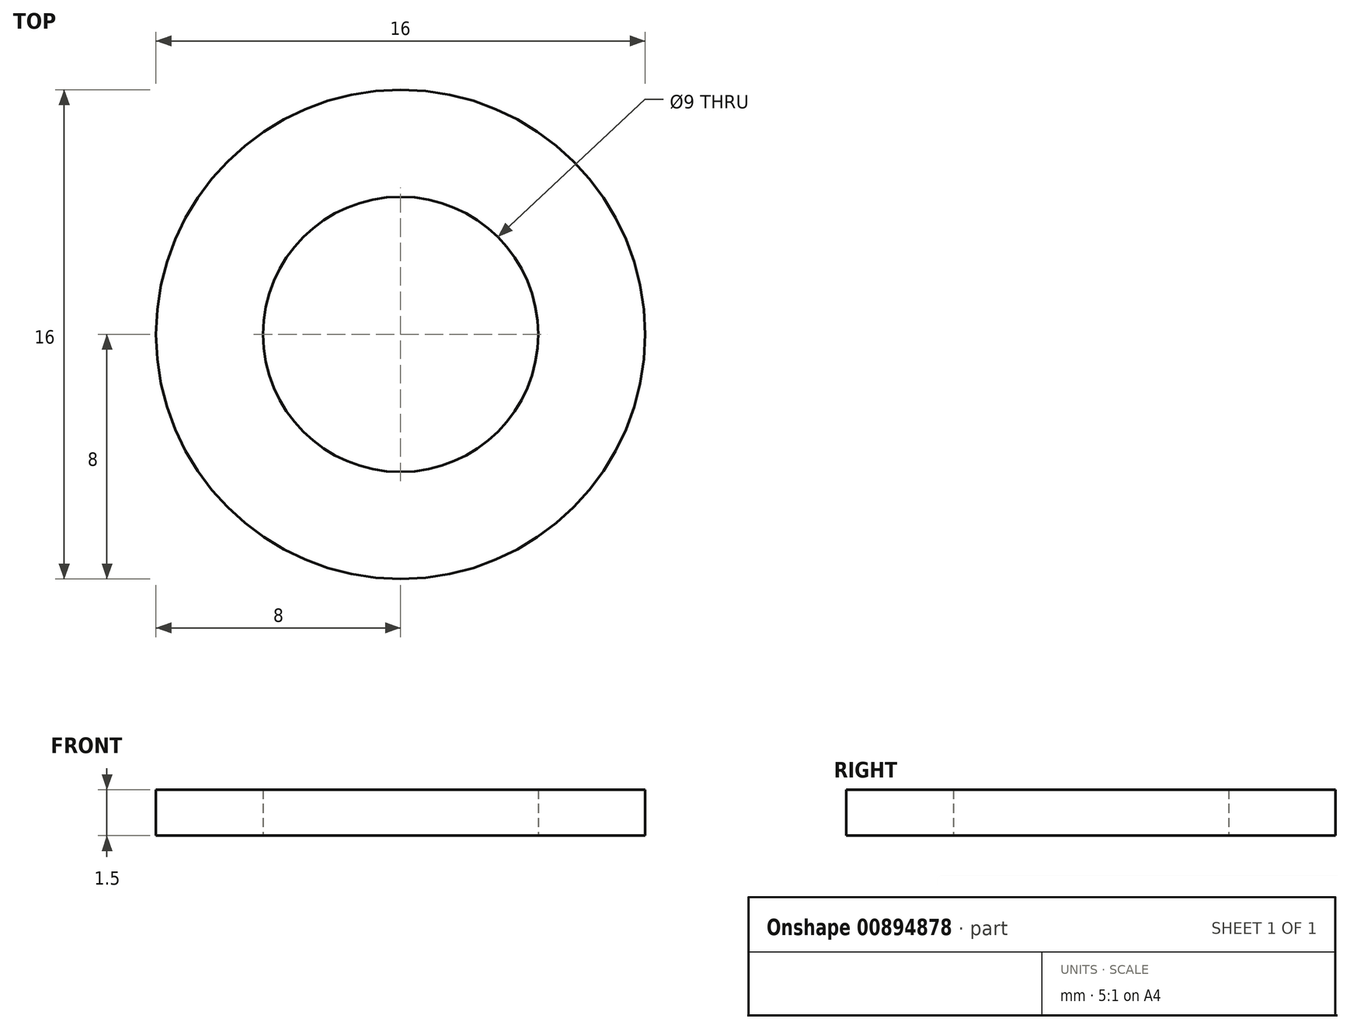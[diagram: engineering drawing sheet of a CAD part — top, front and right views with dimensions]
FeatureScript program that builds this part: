
annotation { "Feature Type Name" : "Feature", "Feature Type Description" : "" }
export const myFeature = defineFeature(function(context is Context, id is Id, definition is map)
    precondition{}
    {
        {
            var Q0;
            Q0=qCreatedBy(makeId("Top.planeOp"),FACE);
            var sketch = newSketch(context, id + "F0", { "sketchPlane" : qUnion([Q0])});
            skCircle(sketch, "E0", {"center": v(0, 0) * mm, "radius": 8 * mm});
            skCircle(sketch, "E1", {"center": v(0, 0) * mm, "radius": 4.5 * mm});
            skSolve(sketch);
        }
        {
            var Q0;
            Q0 = qSketchRegion(id + "F0", true);
            extrude(context, id + "F1", {"entities" : qUnion([Q0]), "depth" : 1.5 * mm, "offsetDistance" : 25 * mm});
        }
    });
